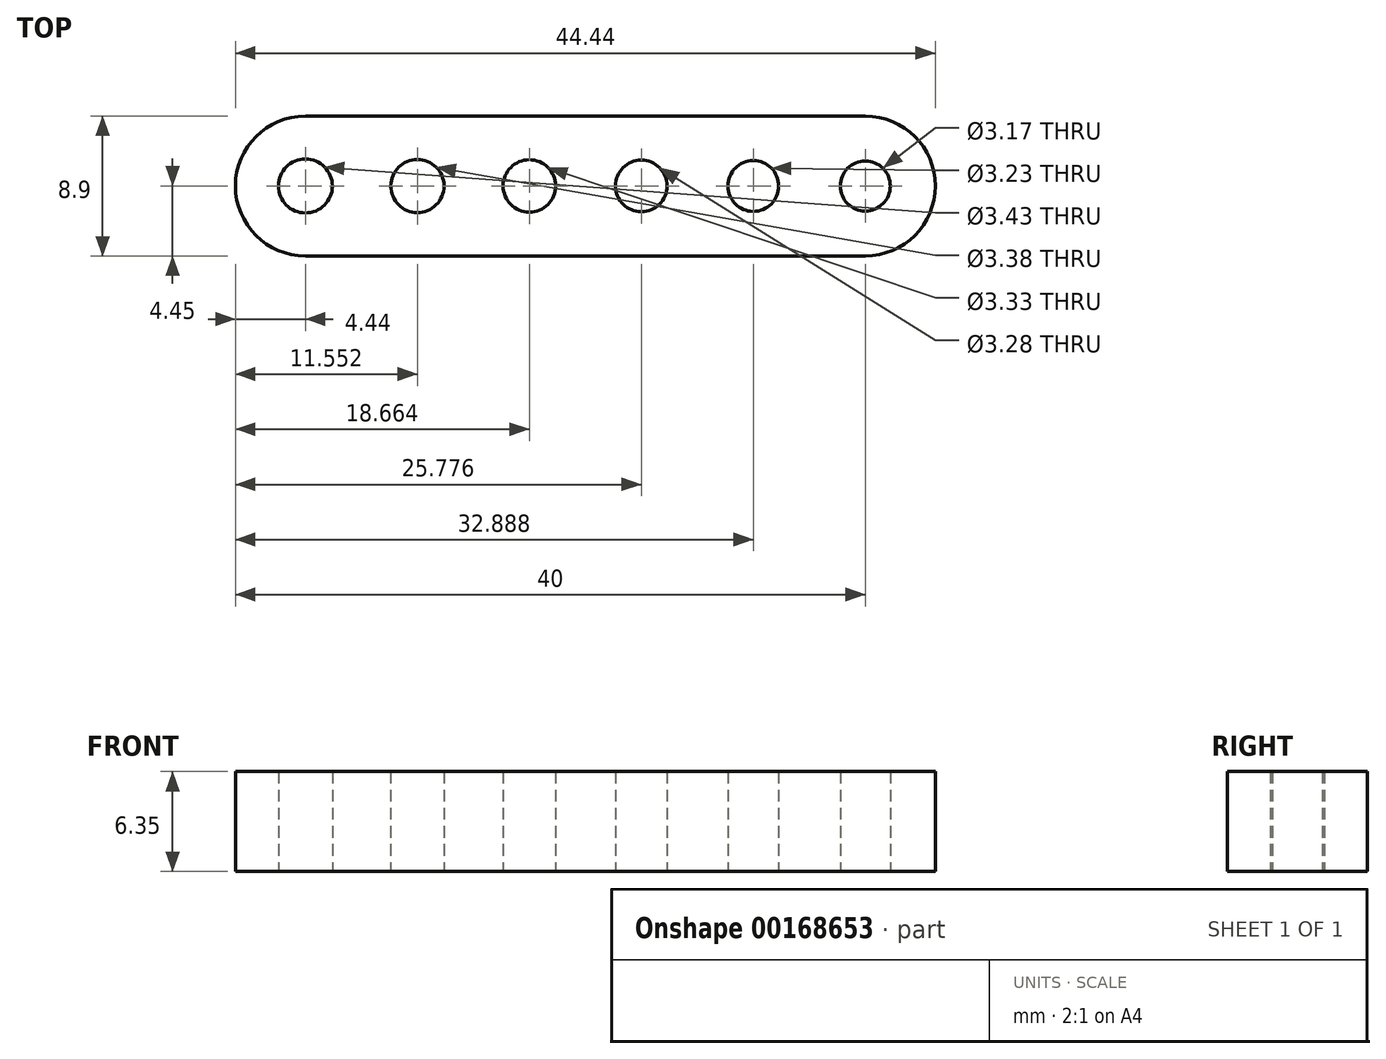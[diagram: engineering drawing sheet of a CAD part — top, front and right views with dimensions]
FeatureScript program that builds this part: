
annotation { "Feature Type Name" : "Feature", "Feature Type Description" : "" }
export const myFeature = defineFeature(function(context is Context, id is Id, definition is map)
    precondition{}
    {
        {
            var Q0;
            Q0=qCreatedBy(makeId("Top.planeOp"),FACE);
            var sketch = newSketch(context, id + "F0", { "sketchPlane" : qUnion([Q0])});
            skLineSegment(sketch, "E0", {"start": v(0, 11.69) * mm, "end": v(0, 0) * mm, "construction": true});
            skLineSegment(sketch, "E1", {"start": v(0, 0) * mm, "end": v(28.65, 0) * mm, "construction": true});
            skLineSegment(sketch, "E2", {"start": v(0, 4.44) * mm, "end": v(17.78, 4.45) * mm});
            skArc(sketch, "E3", {"start": v(17.78, 4.45) * mm, "mid": v(20.92, 3.14) * mm, "end": v(22.22, 0) * mm});
            skArc(sketch, "E4.MirrorCS", {"start": v(17.78, -4.45) * mm, "mid": v(20.92, -3.14) * mm, "end": v(22.22, 0) * mm});
            skLineSegment(sketch, "E5.MirrorCS", {"start": v(0, -4.44) * mm, "end": v(17.78, -4.45) * mm});
            skArc(sketch, "E6.MirrorCS", {"start": v(-17.78, 4.45) * mm, "mid": v(-20.92, 3.14) * mm, "end": v(-22.22, 0) * mm});
            skLineSegment(sketch, "E7.MirrorCS", {"start": v(0, 0) * mm, "end": v(-28.65, 0) * mm, "construction": true});
            skLineSegment(sketch, "E8.MirrorCS", {"start": v(0, 4.44) * mm, "end": v(-17.78, 4.45) * mm});
            skLineSegment(sketch, "E9.MirrorCS", {"start": v(0, -4.44) * mm, "end": v(-17.78, -4.45) * mm});
            skArc(sketch, "E10.MirrorCS", {"start": v(-17.78, -4.45) * mm, "mid": v(-20.92, -3.14) * mm, "end": v(-22.22, 0) * mm});
            skPoint(sketch, "E11.1.0.0", {"position": v(10.67, 0) * mm});
            skPoint(sketch, "E11.2.0.0", {"position": v(3.56, 0) * mm});
            skPoint(sketch, "E11.3.0.0", {"position": v(-3.56, 0) * mm});
            skPoint(sketch, "E11.4.0.0", {"position": v(-10.67, 0) * mm});
            skLineSegment(sketch, "E11.direction1", {"start": v(17.78, 0) * mm, "end": v(10.67, 0) * mm, "construction": true});
            skCircle(sketch, "E12", {"center": v(17.78, 0) * mm, "radius": 1.59 * mm});
            skCircle(sketch, "E13", {"center": v(10.67, 0) * mm, "radius": 1.61 * mm});
            skCircle(sketch, "E14", {"center": v(-17.78, 0) * mm, "radius": 1.71 * mm});
            skCircle(sketch, "E15", {"center": v(-10.67, 0) * mm, "radius": 1.69 * mm});
            skCircle(sketch, "E16", {"center": v(-3.56, 0) * mm, "radius": 1.66 * mm});
            skCircle(sketch, "E17", {"center": v(3.56, 0) * mm, "radius": 1.64 * mm});
            skSolve(sketch);
        }
        {
            var Q0;
            Q0 = qSketchRegion(id + "F0", true);
            extrude(context, id + "F1", {"entities" : qUnion([Q0]), "depth" : 6.35 * mm});
        }
    });
